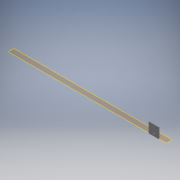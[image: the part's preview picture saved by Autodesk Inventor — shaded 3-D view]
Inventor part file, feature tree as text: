
AUTODESK INVENTOR PART (.ipt)
format: ipt  version: 2016 (Build 200138000, 138)  size: 158,720 bytes
history: native  units: in
note: dims shown in document units (in); Inventor stores cm internally (conversion verified against a paired STEP export)
features: extrude x3, sketch x3, plane x1
ambient origin geometry x8: Origin, YZ Plane, XZ Plane, XY Plane, X Axis, Y Axis, Z Axis, Center Point
bodies: Body1 (feature_tree)
feature tree (7):
  plane  "Work Plane1"
  extrude  "Extrusion3"  Depth=2.0in
  extrude  "Extrusion4"  Depth=2.0in TaperAngle=0.0deg
  extrude  "Extrusion5"  Depth=0.5in
  sketch  "Sketch1"  dims[d0=1.0in d1=2.0in]
  sketch  "Sketch3"  dims[d9=0.125in d10=2.0in d11=0.0in]
  sketch  "Sketch4"  dims[d12=0.2656in d13=0.5in d14=1.0in d15=1.0in d16=0.0in d17=1.0in d18=2.0in d19=0.0in d20=0.25in d21=1.0in d22=0.375in d23=1.0in]
